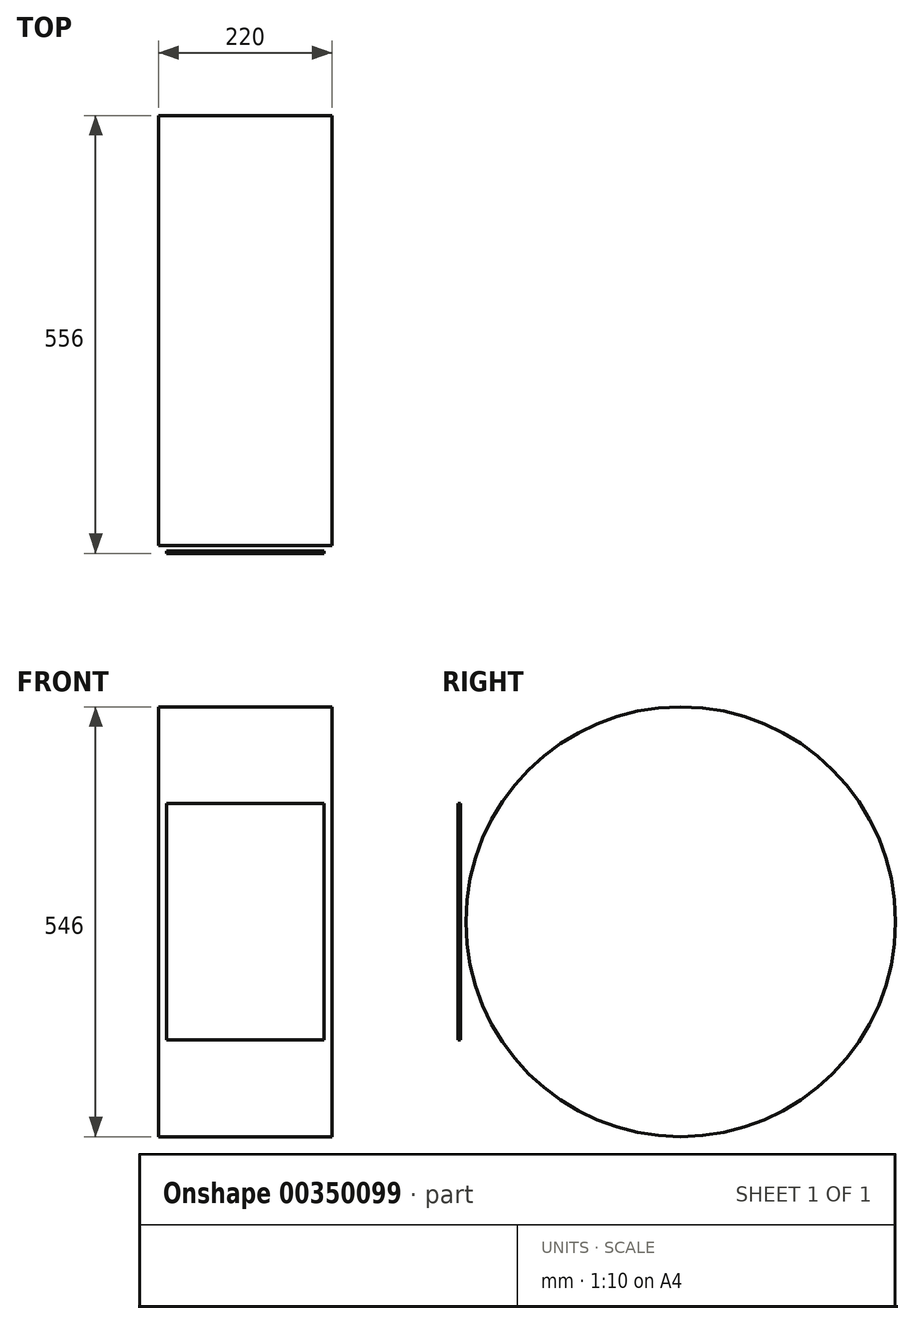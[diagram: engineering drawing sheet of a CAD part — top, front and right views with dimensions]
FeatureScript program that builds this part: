
annotation { "Feature Type Name" : "Feature", "Feature Type Description" : "" }
export const myFeature = defineFeature(function(context is Context, id is Id, definition is map)
    precondition{}
    {
        {
            var Q0;
            Q0=qCreatedBy(makeId("Front.planeOp"),FACE);
            var sketch = newSketch(context, id + "F0", { "sketchPlane" : qUnion([Q0])});
            skLineSegment(sketch, "E0.bottom", {"start": v(-100, 150) * mm, "end": v(100, 150) * mm});
            skLineSegment(sketch, "E0.top", {"start": v(-100, -150) * mm, "end": v(100, -150) * mm});
            skLineSegment(sketch, "E0.left", {"start": v(-100, 150) * mm, "end": v(-100, -150) * mm});
            skLineSegment(sketch, "E0.right", {"start": v(100, 150) * mm, "end": v(100, -150) * mm});
            skLineSegment(sketch, "E1", {"start": v(-100, 150) * mm, "end": v(100, -150) * mm, "construction": true});
            skSolve(sketch);
        }
        {
            var Q0;
            Q0 = qSketchRegion(id + "F0", true);
            extrude(context, id + "F1", {"entities" : qUnion([Q0]), "depth" : 3 * mm});
        }
        {
            var Q0;
            Q0=qCreatedBy(makeId("Right.planeOp"),FACE);
            var sketch = newSketch(context, id + "F2", { "sketchPlane" : qUnion([Q0])});
            skCircle(sketch, "E2", {"center": v(280, 0) * mm, "radius": 273 * mm});
            skLineSegment(sketch, "E3", {"start": v(280, 0) * mm, "end": v(0, 0) * mm, "construction": true});
            skSolve(sketch);
        }
        {
            var Q0;
            Q0 = qSketchRegion(id + "F2", true);
            extrude(context, id + "F3", {"entities" : qUnion([Q0]), "depth" : 110 * mm, "hasSecondDirection" : true, "secondDirectionOppositeDirection" : true, "secondDirectionDepth" : 110 * mm});
        }
    });
